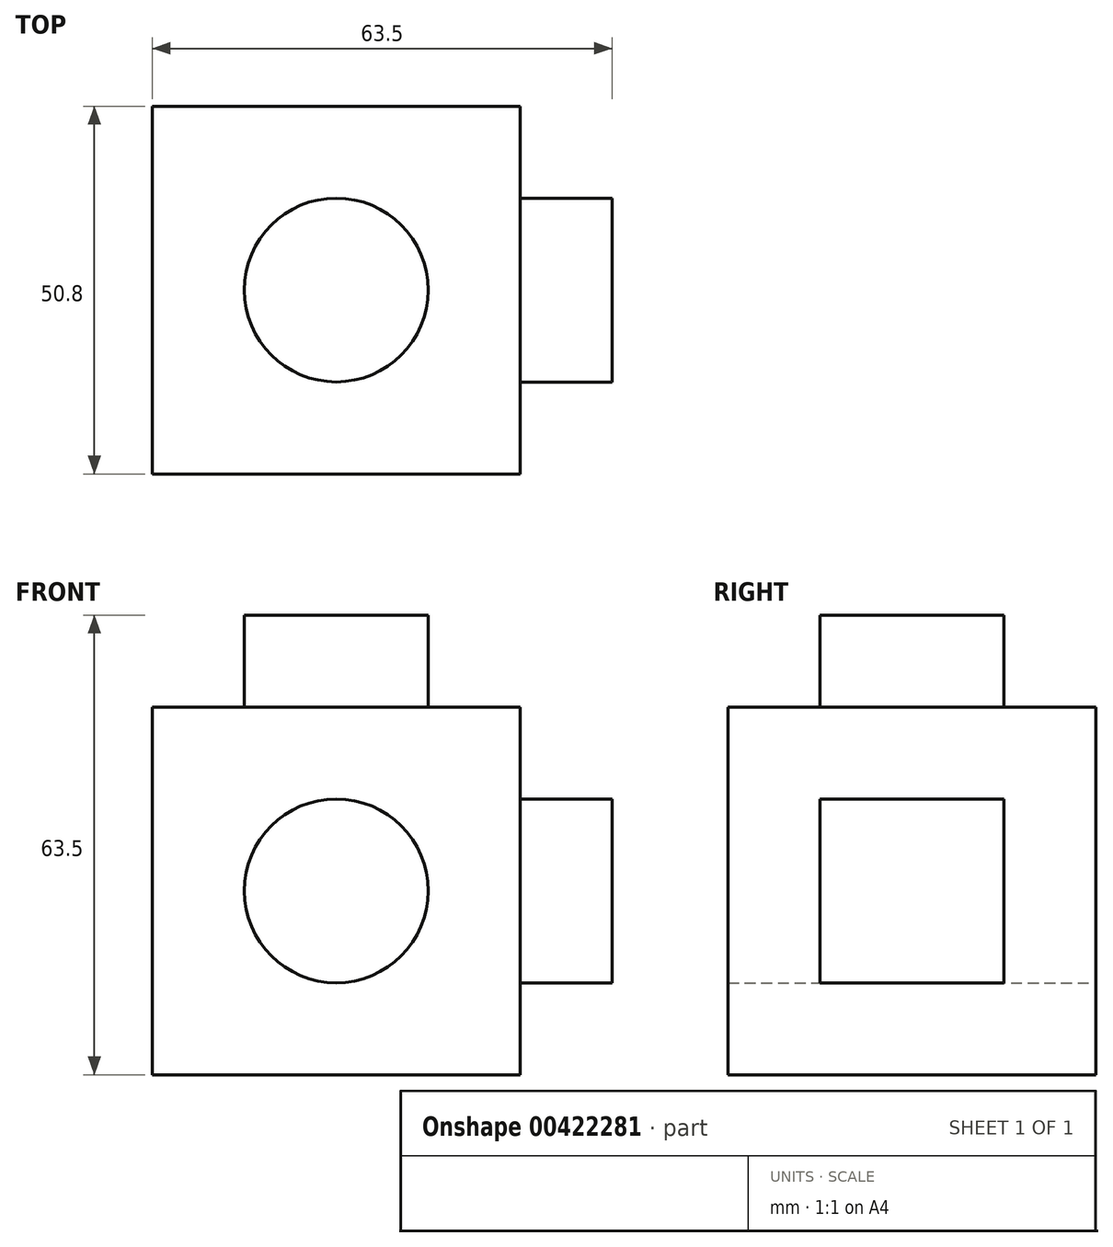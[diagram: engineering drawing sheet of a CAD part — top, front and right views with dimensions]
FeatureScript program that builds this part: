
annotation { "Feature Type Name" : "Feature", "Feature Type Description" : "" }
export const myFeature = defineFeature(function(context is Context, id is Id, definition is map)
    precondition{}
    {
        {
            var Q0;
            Q0=qCreatedBy(makeId("Front.planeOp"),FACE);
            var sketch = newSketch(context, id + "F0", { "sketchPlane" : qUnion([Q0])});
            skLineSegment(sketch, "E0.bottom", {"start": v(0, 0) * mm, "end": v(-50.8, 0) * mm});
            skLineSegment(sketch, "E0.top", {"start": v(0, 50.8) * mm, "end": v(-50.8, 50.8) * mm});
            skLineSegment(sketch, "E0.left", {"start": v(0, 0) * mm, "end": v(0, 50.8) * mm});
            skLineSegment(sketch, "E0.right", {"start": v(-50.8, 0) * mm, "end": v(-50.8, 50.8) * mm});
            skCircle(sketch, "E1", {"center": v(-25.4, 25.4) * mm, "radius": 12.7 * mm});
            skSolve(sketch);
        }
        {
            var Q0;
            Q0=makeQuery(id+"F0.imprint","IMPRINT",FACE,{"disambiguationData":[TD([[makeQuery(id+"F0.imprint","IMPRINT",EDGE,{"derivedFrom":sQuery(id+"F0.wireOp",EDGE,"E0.bottom")}),-1.0]])]});
            extrude(context, id + "F1", {"entities" : qUnion([Q0]), "depth" : 50.8 * mm});
        }
        {
            var Q0;
            Q0=qCreatedBy(makeId("Right.planeOp"),FACE);
            var sketch = newSketch(context, id + "F2", { "sketchPlane" : qUnion([Q0])});
            skLineSegment(sketch, "E2.bottom", {"start": v(-38.1, 38.1) * mm, "end": v(-12.7, 38.1) * mm});
            skLineSegment(sketch, "E2.top", {"start": v(-38.1, 12.7) * mm, "end": v(-12.7, 12.7) * mm});
            skLineSegment(sketch, "E2.left", {"start": v(-38.1, 38.1) * mm, "end": v(-38.1, 12.7) * mm});
            skLineSegment(sketch, "E2.right", {"start": v(-12.7, 38.1) * mm, "end": v(-12.7, 12.7) * mm});
            skSolve(sketch);
        }
        {
            var Q0;
            Q0=makeQuery(id+"F2.imprint","IMPRINT",FACE,{"disambiguationData":[TD([[makeQuery(id+"F2.imprint","IMPRINT",EDGE,{"derivedFrom":sQuery(id+"F2.wireOp",EDGE,"E2.bottom")}),-1.0]])]});
            extrude(context, id + "F3", {"entities" : qUnion([Q0]), "operationType" : NewBodyOperationType.ADD, "depth" : 12.7 * mm});
        }
        {
            var Q0;
            Q0=makeQuery(id+"F1.opExtrude","SWEPT_FACE",FACE,{"disambiguationData":[OSD([sQuery(id+"F0.wireOp",EDGE,"E0.top")])]});
            var sketch = newSketch(context, id + "F4", { "sketchPlane" : qUnion([Q0])});
            skCircle(sketch, "E3", {"center": v(-25.4, -25.4) * mm, "radius": 12.7 * mm});
            skSolve(sketch);
        }
        {
            var Q0;
            Q0=makeQuery(id+"F4.imprint","IMPRINT",FACE,{"disambiguationData":[TD([[makeQuery(id+"F4.imprint","IMPRINT",EDGE,{"derivedFrom":sQuery(id+"F4.wireOp",EDGE,"E3")}),1.0]])]});
            extrude(context, id + "F5", {"entities" : qUnion([Q0]), "operationType" : NewBodyOperationType.ADD, "depth" : 12.7 * mm});
        }
    });
